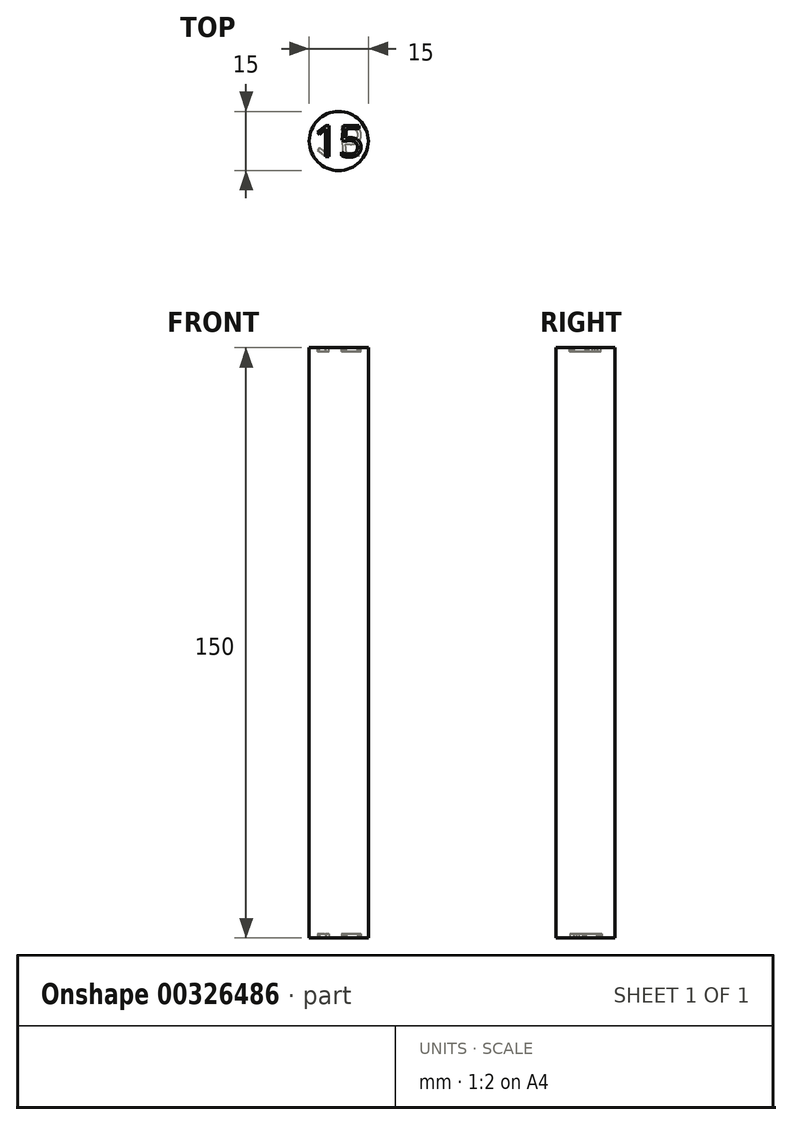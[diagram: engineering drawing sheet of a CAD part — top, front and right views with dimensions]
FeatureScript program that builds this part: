
annotation { "Feature Type Name" : "Feature", "Feature Type Description" : "" }
export const myFeature = defineFeature(function(context is Context, id is Id, definition is map)
    precondition{}
    {
        {
            var Q0;
            Q0=qCreatedBy(makeId("Top.planeOp"),FACE);
            var sketch = newSketch(context, id + "F0", { "sketchPlane" : qUnion([Q0])});
            skCircle(sketch, "E0", {"center": v(0, 0) * mm, "radius": 7.5 * mm});
            skSolve(sketch);
        }
        {
            var Q0;
            Q0 = qSketchRegion(id + "F0", true);
            extrude(context, id + "F1", {"entities" : qUnion([Q0]), "depth" : 150 * mm});
        }
        {
            var Q0;
            Q0=makeQuery(id+"F1.opExtrude","CAP_FACE",FACE,{"disambiguationData":[OSD([sQuery(id+"F0.wireOp",EDGE,"E0")])],"isStart":true});
            var sketch = newSketch(context, id + "F2", { "sketchPlane" : qUnion([Q0])});
            skText(sketch, "E1", { "text": "15", "fontName": "OpenSans-Regular.ttf"});
            const initialGuessF2  = {"E1": [-0.0064, -0.004, 1, 0, 0.008]};
            skSetInitialGuess(sketch, initialGuessF2);
            skSolve(sketch);
        }
        {
            var Q0;
            Q0 = qSketchRegion(id + "F2", true);
            extrude(context, id + "F3", {"entities" : qUnion([Q0]), "operationType" : NewBodyOperationType.REMOVE, "oppositeDirection" : true, "depth" : 1 * mm});
        }
        {
            var Q0;
            Q0=makeQuery(id+"F1.opExtrude","CAP_FACE",FACE,{"disambiguationData":[OSD([sQuery(id+"F0.wireOp",EDGE,"E0")])],"isStart":false});
            var sketch = newSketch(context, id + "F4", { "sketchPlane" : qUnion([Q0])});
            skText(sketch, "E2", { "text": "15", "fontName": "OpenSans-Regular.ttf"});
            const initialGuessF4  = {"E2": [-0.0064, -0.004, 1, 0, 0.008]};
            skSetInitialGuess(sketch, initialGuessF4);
            skSolve(sketch);
        }
        {
            var Q0;
            Q0 = qSketchRegion(id + "F4", true);
            extrude(context, id + "F5", {"entities" : qUnion([Q0]), "operationType" : NewBodyOperationType.REMOVE, "oppositeDirection" : true, "depth" : 1 * mm});
        }
    });
